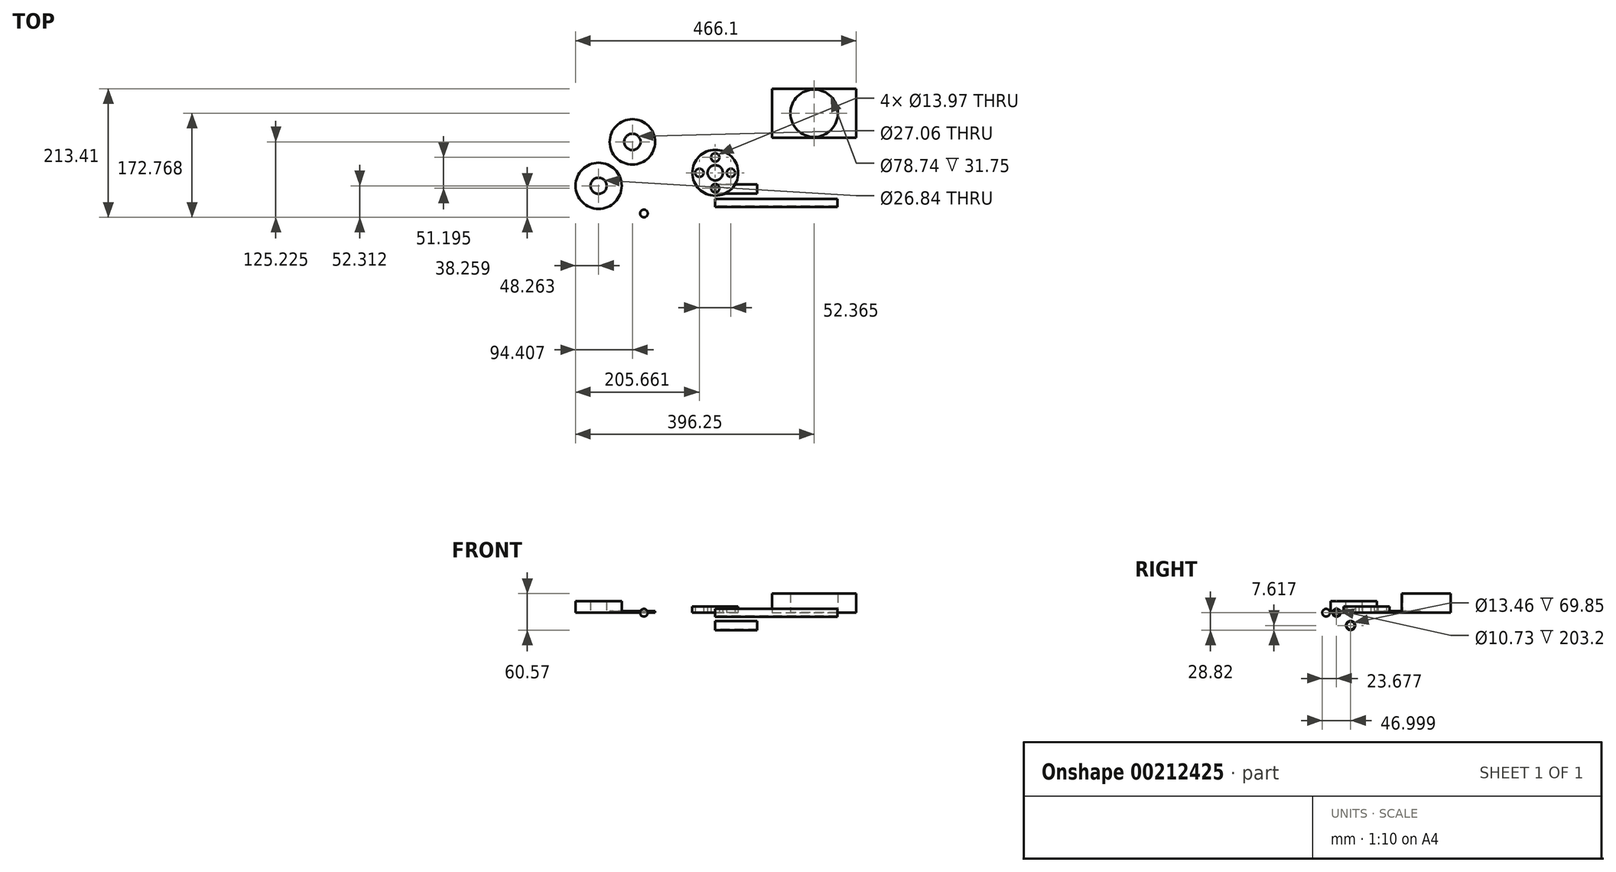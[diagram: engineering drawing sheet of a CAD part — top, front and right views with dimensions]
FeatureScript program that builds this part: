
annotation { "Feature Type Name" : "Feature", "Feature Type Description" : "" }
export const myFeature = defineFeature(function(context is Context, id is Id, definition is map)
    precondition{}
    {
        {
            var Q0;
            Q0=qCreatedBy(makeId("Top.planeOp"),FACE);
            var sketch = newSketch(context, id + "F0", { "sketchPlane" : qUnion([Q0])});
            skCircle(sketch, "E0", {"center": v(0, 0) * mm, "radius": 38.1 * mm});
            skCircle(sketch, "E1", {"center": v(0, 0) * mm, "radius": 12.7 * mm});
            skCircle(sketch, "E2", {"center": v(-26.33, 0) * mm, "radius": 6.99 * mm});
            skCircle(sketch, "E3", {"center": v(0, 25.6) * mm, "radius": 6.99 * mm});
            skCircle(sketch, "E4", {"center": v(26.04, 0) * mm, "radius": 6.99 * mm});
            skCircle(sketch, "E5", {"center": v(0, -25.6) * mm, "radius": 6.99 * mm});
            skSolve(sketch);
        }
        {
            var Q0;
            Q0 = qSketchRegion(id + "F0", true);
            extrude(context, id + "F1", {"entities" : qUnion([Q0]), "depth" : 10.16 * mm});
        }
        {
            var Q0;
            Q0=qCreatedBy(makeId("Top.planeOp"),FACE);
            var sketch = newSketch(context, id + "F2", { "sketchPlane" : qUnion([Q0])});
            skCircle(sketch, "E6", {"center": v(-137.58, 51.37) * mm, "radius": 37.68 * mm});
            skCircle(sketch, "E7", {"center": v(-137.58, 51.37) * mm, "radius": 13.53 * mm});
            skLineSegment(sketch, "E8", {"start": v(-99.96, 53.43) * mm, "end": v(-175.2, 49.3) * mm});
            skLineSegment(sketch, "E9", {"start": v(-99.93, 52.87) * mm, "end": v(-124.06, 51.69) * mm});
            skLineSegment(sketch, "E10", {"start": v(-151.06, 50.13) * mm, "end": v(-175.18, 48.8) * mm});
            skSolve(sketch);
        }
        {
            var Q0;
            Q0 = qSketchRegion(id + "F2", true);
            extrude(context, id + "F3", {"entities" : qUnion([Q0]), "depth" : 2.54 * mm});
        }
        {
            var Q0;
            Q0=qCreatedBy(makeId("Top.planeOp"),FACE);
            var sketch = newSketch(context, id + "F4", { "sketchPlane" : qUnion([Q0])});
            skArc(sketch, "E11", {"start": v(-118.48, -73.86) * mm, "mid": v(-112.13, -67.5) * mm, "end": v(-118.48, -61.16) * mm});
            skLineSegment(sketch, "E12", {"start": v(-118.48, -73.86) * mm, "end": v(-118.48, -61.16) * mm});
            skSolve(sketch);
        }
        {
            var Q0;
            Q0=makeQuery(id+"F4.imprint","IMPRINT",FACE,{"disambiguationData":[TD([[makeQuery(id+"F4.imprint","IMPRINT",EDGE,{"derivedFrom":sQuery(id+"F4.wireOp",EDGE,"E11")}),1.0]])]});
            var Q1;
            Q1=sQuery(id+"F4.wireOp",EDGE,"E12");
            revolve(context, id + "F5", {"entities" : qUnion([Q0]), "axis" : qUnion([Q1]), "revolveType" : RevolveType.FULL});
        }
        {
            var Q0;
            Q0=qCreatedBy(makeId("Right.planeOp"),FACE);
            var sketch = newSketch(context, id + "F6", { "sketchPlane" : qUnion([Q0])});
            skCircle(sketch, "E13", {"center": v(-50.18, 0) * mm, "radius": 6.63 * mm});
            skCircle(sketch, "E14", {"center": v(-50.18, 0) * mm, "radius": 5.36 * mm});
            skSolve(sketch);
        }
        {
            var Q0;
            Q0=makeQuery(id+"F6.imprint","IMPRINT",FACE,{"disambiguationData":[TD([[makeQuery(id+"F6.imprint","IMPRINT",EDGE,{"derivedFrom":sQuery(id+"F6.wireOp",EDGE,"E13")}),1.0]])]});
            extrude(context, id + "F7", {"entities" : qUnion([Q0]), "depth" : 203.2 * mm});
        }
        {
            var Q0;
            Q0=qCreatedBy(makeId("Top.planeOp"),FACE);
            var sketch = newSketch(context, id + "F8", { "sketchPlane" : qUnion([Q0])});
            skCircle(sketch, "E15", {"center": v(-193.73, -21.55) * mm, "radius": 38.26 * mm});
            skCircle(sketch, "E16", {"center": v(-193.73, -21.55) * mm, "radius": 13.42 * mm});
            skSolve(sketch);
        }
        {
            var Q0;
            Q0=makeQuery(id+"F8.imprint","IMPRINT",FACE,{"disambiguationData":[TD([[makeQuery(id+"F8.imprint","IMPRINT",EDGE,{"derivedFrom":sQuery(id+"F8.wireOp",EDGE,"E15")}),1.0]])]});
            extrude(context, id + "F9", {"entities" : qUnion([Q0]), "depth" : 19.05 * mm});
        }
        {
            var Q0;
            Q0=qCreatedBy(makeId("Top.planeOp"),FACE);
            var sketch = newSketch(context, id + "F10", { "sketchPlane" : qUnion([Q0])});
            skLineSegment(sketch, "E17.bottom", {"start": v(94.4, 139.55) * mm, "end": v(234.1, 139.55) * mm});
            skLineSegment(sketch, "E17.top", {"start": v(94.4, 58.27) * mm, "end": v(234.1, 58.27) * mm});
            skLineSegment(sketch, "E17.left", {"start": v(94.4, 139.55) * mm, "end": v(94.4, 58.27) * mm});
            skLineSegment(sketch, "E17.right", {"start": v(234.1, 139.55) * mm, "end": v(234.1, 58.27) * mm});
            skCircle(sketch, "E18", {"center": v(164.26, 98.9) * mm, "radius": 39.37 * mm});
            skSolve(sketch);
        }
        {
            var Q0;
            Q0=makeQuery(id+"F10.imprint","IMPRINT",FACE,{"disambiguationData":[TD([[makeQuery(id+"F10.imprint","IMPRINT",EDGE,{"derivedFrom":sQuery(id+"F10.wireOp",EDGE,"E17.bottom")}),-1.0]])]});
            extrude(context, id + "F11", {"entities" : qUnion([Q0]), "depth" : 31.75 * mm});
        }
        {
            var Q0;
            Q0=qCreatedBy(makeId("Right.planeOp"),FACE);
            var sketch = newSketch(context, id + "F12", { "sketchPlane" : qUnion([Q0])});
            skCircle(sketch, "E19", {"center": v(-26.86, -21.2) * mm, "radius": 6.73 * mm});
            skCircle(sketch, "E20", {"center": v(-26.86, -21.2) * mm, "radius": 7.62 * mm});
            skSolve(sketch);
        }
        {
            var Q0;
            Q0=makeQuery(id+"F12.imprint","IMPRINT",FACE,{"disambiguationData":[TD([[makeQuery(id+"F12.imprint","IMPRINT",EDGE,{"derivedFrom":sQuery(id+"F12.wireOp",EDGE,"E19")}),-1.0]])]});
            extrude(context, id + "F13", {"entities" : qUnion([Q0]), "depth" : 69.85 * mm});
        }
    });
